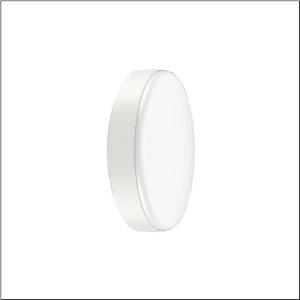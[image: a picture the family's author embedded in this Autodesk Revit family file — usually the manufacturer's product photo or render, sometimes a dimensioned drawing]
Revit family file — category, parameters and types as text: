
# Revit family: rondel_31_51wc10db34a
name_source: partatom
category: Lighting Fixtures
units: mm (PartAtom-declared; Revit-internal decimal feet)

## family parameters
Cut with Voids When Loaded = No
Host = Face
Light Source = No
Part Type = Normal
Room Calculation Point = No
Round Connector Dimension = Use Diameter
Shared = No

## types (1)
- Rondel 31 (1 x LED, 4250 lm, 34 W, 3000K)
    Apparent Load = 34 VA
    CIE Flux Codes = 44 75 94 94 100
    Color Rendering = 80
    Color Temperature = 3000K
    Default Elevation = 1800 mm
    Description = Rondel 31, wall and ceiling luminaire, primary optical cover: cover, of PC, opal, light emission: direct distribution, primary light characteristic: symmetric, installation type: surface-mounted, LED, rated luminous flux: 4.250lm, luminous efficacy: 125lm/W, light colour: 830, colour temperature: 3000K, with terminal, 5-pole, max. 2.5mm², mains connection: 220..240V, AC, 50/60Hz, rated input power: 34W, luminaire housing, of PC, traffic white (RAL 9016), diameter: 480mm, protection rating (complete): IP65, insulation class (complete): insulation class II (safety insulation), certification: CE, impact resistance: IK10, permissible operating ambient temperature: -20..+40°C, permissible storage temperature: -20..+60°C, packaging unit: 1 piece
    Height = 97 mm
    Lamp = 1 x LED
    Lamp Light Flux = 4250 lm
    Lamp Power = 34 W
    Lamp count = 1
    Length = 480 mm
    Luminous efficacy = 125 lm/W
    Manufacturer = Siteco
    ModVariant = No
    Model = 51WC10DB34A
    Mounting Place = Ceiling
    Mounting Type = Surface mounted
    Number of Poles = 1
    OnlyDefault = Yes
    Power Factor = 1
    Product Name = Rondel 31
    Product group = wall and ceiling luminaire
    ProductGroupID = 302
    Protection Class = Protection class II
    Protection Degree = IP 65
    RLX_Detail_Level = 1
    RLX_Emergency_Light_Flux = 0 lm
    RLX_Emergency_Type = 0
    RLX_Emergency_Type_DB = No
    RlxData = <blob elided: 40793 chars, md5=608dfbd9>
    Socket = socket
    Standby Power = 0 W
    System Light Flux = 4250 lm
    System Power = 34 W
    Type Comments = Product without accessories
    Type Image = l_1007188.jpg
    URL = http://relux.com
    VarID = ---
    Voltage = 0 V
    Weight = 0.00 kg
    Width = 0 mm  [stored 0 ft]

note: [stored X ft] marks values corroborated as IEEE doubles in the binary element streams (Revit-internal decimal feet)

## geometry (parser evidence)
native form markers: Blend x4, Sweep x13
no freeform markers — native parametric forms only
